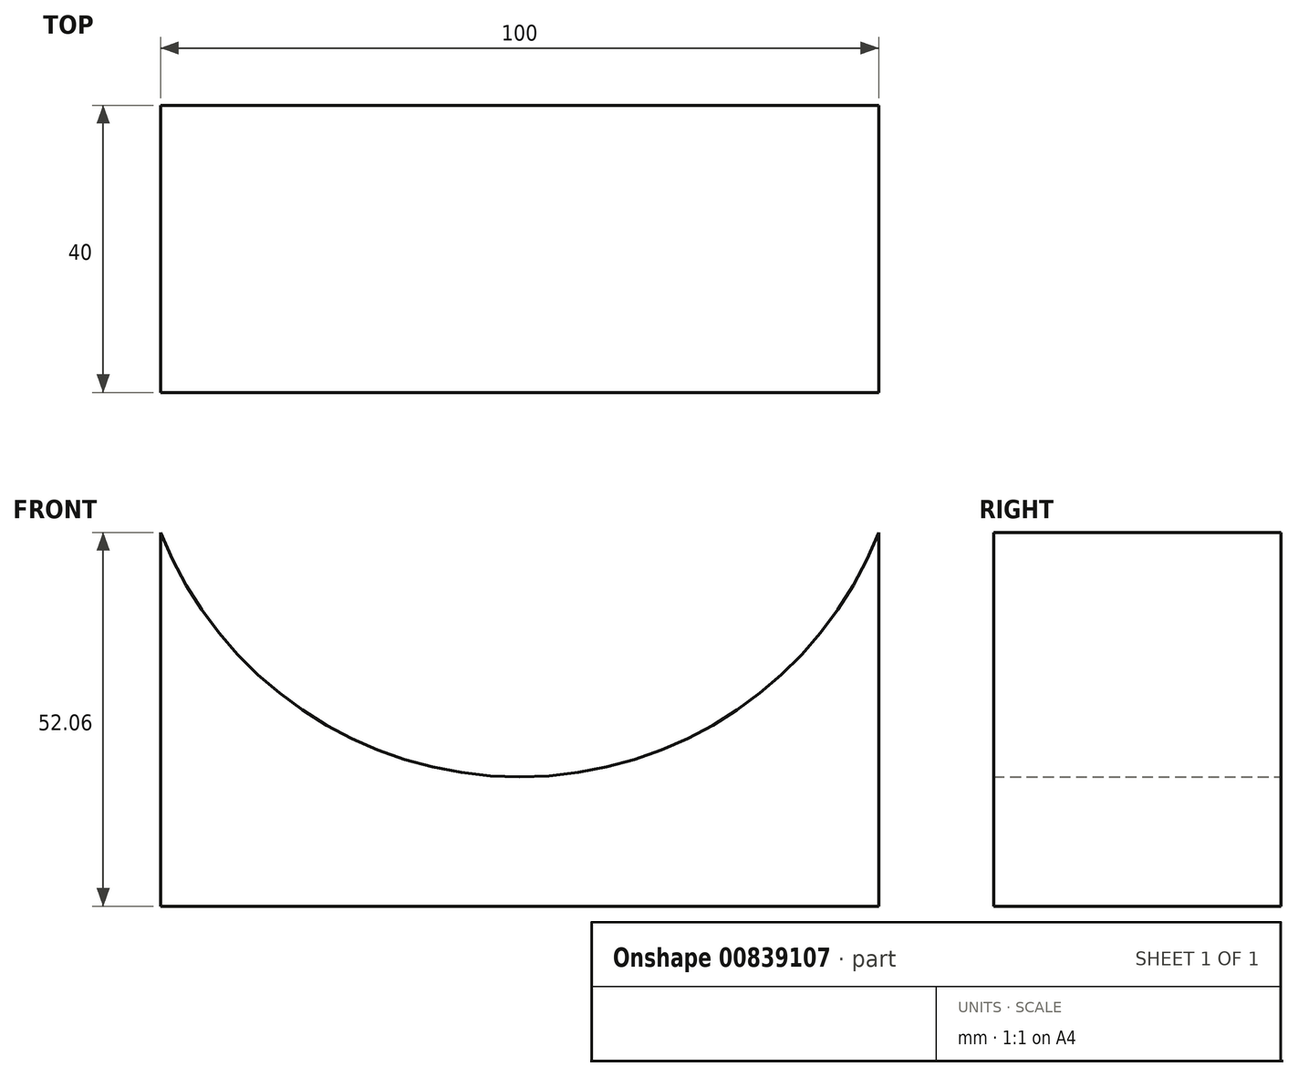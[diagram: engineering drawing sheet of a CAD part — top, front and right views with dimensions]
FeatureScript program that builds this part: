
annotation { "Feature Type Name" : "Feature", "Feature Type Description" : "" }
export const myFeature = defineFeature(function(context is Context, id is Id, definition is map)
    precondition{}
    {
        {
            var Q0;
            Q0=qCreatedBy(makeId("Front.planeOp"),FACE);
            var sketch = newSketch(context, id + "F0", { "sketchPlane" : qUnion([Q0])});
            skLineSegment(sketch, "E0", {"start": v(-56.37, 21.08) * mm, "end": v(-56.37, -30.98) * mm});
            skLineSegment(sketch, "E1", {"start": v(-56.37, -30.98) * mm, "end": v(43.63, -30.98) * mm});
            skLineSegment(sketch, "E2", {"start": v(43.63, -30.98) * mm, "end": v(43.63, 21.08) * mm});
            skArc(sketch, "E3", {"start": v(-56.37, 21.08) * mm, "mid": v(-6.37, -12.98) * mm, "end": v(43.63, 21.08) * mm});
            skPoint(sketch, "E4", {"position": v(-6.37, -12.98) * mm});
            skPoint(sketch, "E5", {"position": v(-6.37, -30.98) * mm});
            skSolve(sketch);
        }
        {
            var Q0;
            Q0=makeQuery(id+"F0.imprint","IMPRINT",FACE,{"disambiguationData":[TD([[makeQuery(id+"F0.imprint","IMPRINT",EDGE,{"derivedFrom":sQuery(id+"F0.wireOp",EDGE,"E0")}),1.0]])]});
            extrude(context, id + "F1", {"entities" : qUnion([Q0]), "endBound" : BoundingType.SYMMETRIC, "depth" : 40 * mm, "offsetDistance" : 25 * mm});
        }
    });
